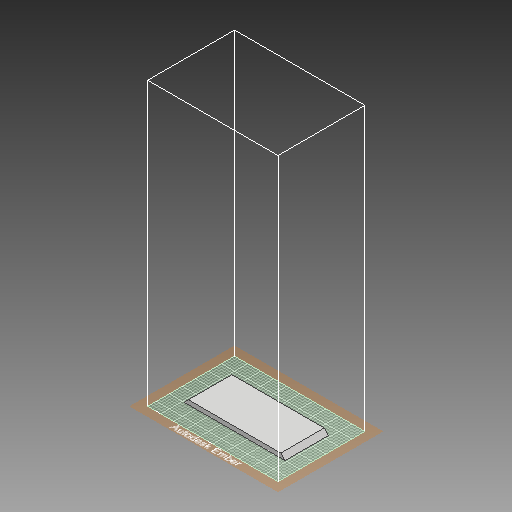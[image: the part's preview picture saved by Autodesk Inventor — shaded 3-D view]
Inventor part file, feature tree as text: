
AUTODESK INVENTOR PART (.ipt)
format: ipt  version: 2018 (Build 220112000, 112)  size: 196,608 bytes
history: native  units: mm
features: extrude x2, sketch x2
ambient origin geometry x8: Origin, YZ Plane, XZ Plane, XY Plane, X Axis, Y Axis, Z Axis, Center Point
bodies: Solid1 (feature_tree)
feature tree (4):
  extrude  "Extrusion1"  Depth=20.0mm
  extrude  "Extrusion2"  Depth=2.0mm
  sketch  "Sketch1"  dims[d0=43.0mm d1=20.0mm]
  sketch  "Sketch2"  dims[d2=2.0mm d3=0.0mm d4=2.0mm d5=2.0mm d6=20.0mm d7=0.0mm]
